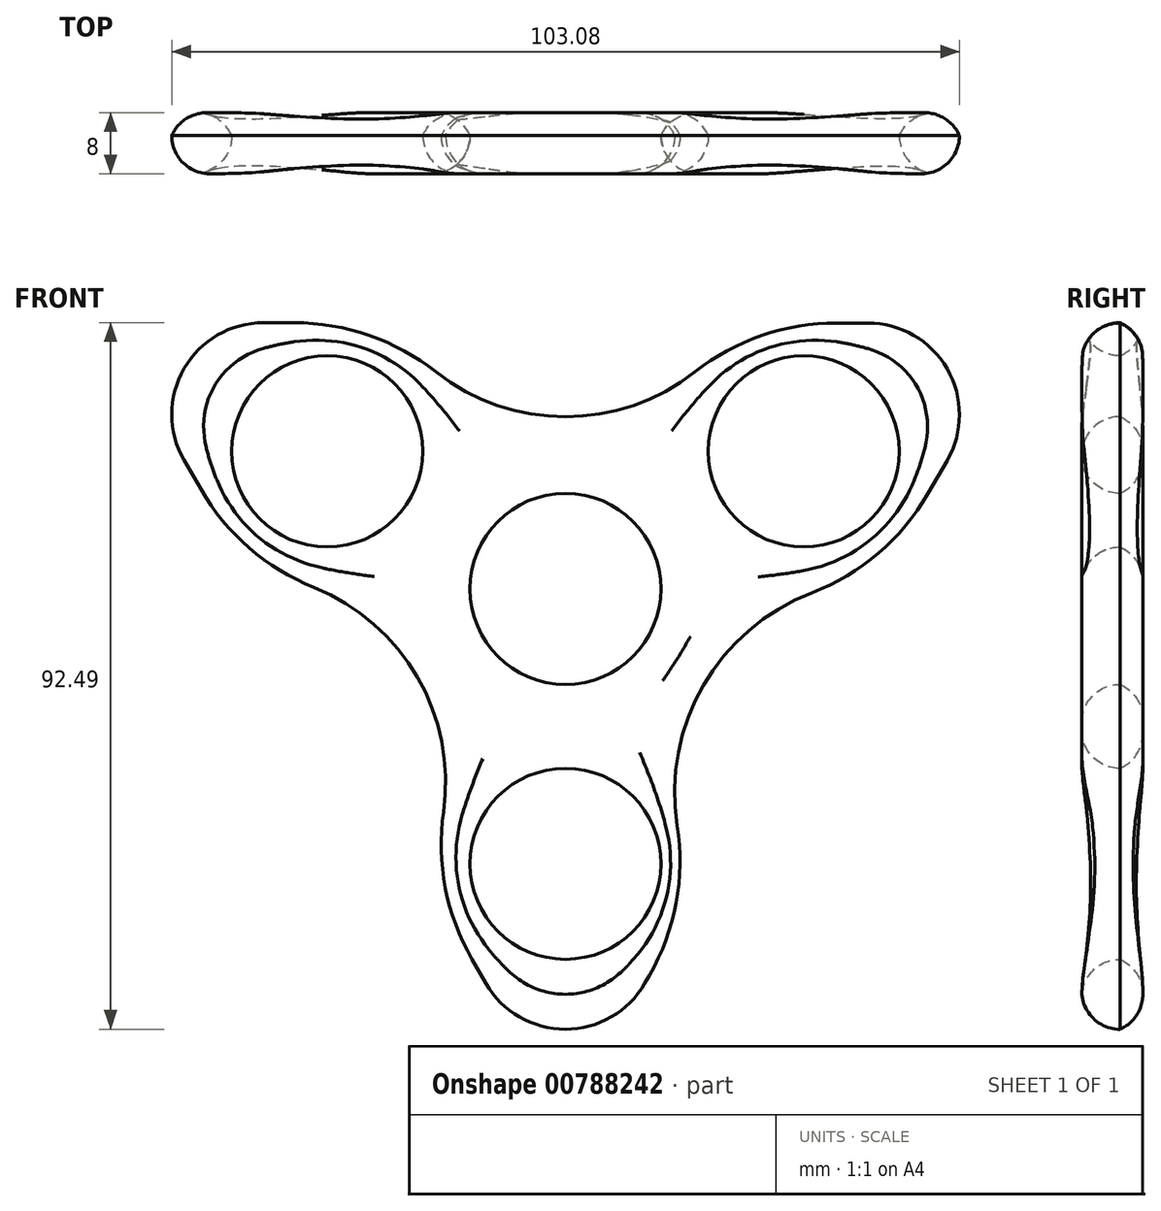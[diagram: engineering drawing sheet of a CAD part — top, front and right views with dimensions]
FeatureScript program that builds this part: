
annotation { "Feature Type Name" : "Feature", "Feature Type Description" : "" }
export const myFeature = defineFeature(function(context is Context, id is Id, definition is map)
    precondition{}
    {
        {
            var Q0;
            Q0=qCreatedBy(makeId("Front.planeOp"),FACE);
            var sketch = newSketch(context, id + "F0", { "sketchPlane" : qUnion([Q0])});
            skCircle(sketch, "E0", {"center": v(0, 0) * mm, "radius": 12.5 * mm});
            skCircle(sketch, "E1", {"center": v(31.18, 18) * mm, "radius": 12.5 * mm});
            skCircle(sketch, "E2", {"center": v(-31.18, 18) * mm, "radius": 12.5 * mm});
            skCircle(sketch, "E3", {"center": v(0, -36) * mm, "radius": 12.5 * mm});
            skCircle(sketch, "E4.cCircle", {"center": v(0, 0) * mm, "radius": 34.83 * mm, "construction": true});
            skLineSegment(sketch, "E4.0", {"start": v(49.94, 16.8) * mm, "end": v(10.37, -51.66) * mm});
            skLineSegment(sketch, "E4.1", {"start": v(-10.41, -51.65) * mm, "end": v(-49.92, 16.85) * mm});
            skLineSegment(sketch, "E4.2", {"start": v(-39.52, 34.84) * mm, "end": v(39.55, 34.81) * mm});
            skPoint(sketch, "E5", {"position": v(30.15, -17.43) * mm});
            skPoint(sketch, "E6", {"position": v(-31.7, 59.94) * mm});
            skArc(sketch, "E7.filletArc", {"start": v(-10.41, -51.65) * mm, "mid": v(-0.02, -57.65) * mm, "end": v(10.37, -51.66) * mm});
            skPoint(sketch, "E8.visualSharp", {"position": v(-24.14, 73.04) * mm});
            skArc(sketch, "E8.filletArc", {"start": v(49.94, 16.8) * mm, "mid": v(49.94, 28.8) * mm, "end": v(39.55, 34.81) * mm});
            skPoint(sketch, "E9.visualSharp", {"position": v(-60.3, 34.85) * mm});
            skArc(sketch, "E9.filletArc", {"start": v(-39.52, 34.84) * mm, "mid": v(-49.92, 28.85) * mm, "end": v(-49.92, 16.85) * mm});
            skCircle(sketch, "E10", {"center": v(42.27, -26.64) * mm, "radius": 27.98 * mm});
            skCircle(sketch, "E11", {"center": v(0, 50) * mm, "radius": 27.46 * mm});
            skCircle(sketch, "E12", {"center": v(-43.15, -25.3) * mm, "radius": 27.46 * mm});
            skCircle(sketch, "E13.cCircle", {"center": v(0, 0) * mm, "radius": 49.97 * mm, "construction": true});
            skSolve(sketch);
        }
        {
            var Q0;
            Q0=makeQuery(id+"F0.imprint","IMPRINT",FACE,{"disambiguationData":[TD([[makeQuery(id+"F0.imprint","IMPRINT",EDGE,{"derivedFrom":sQuery(id+"F0.wireOp",EDGE,"E0")}),-1.0]])]});
            extrude(context, id + "F1", {"entities" : qUnion([Q0]), "endBound" : BoundingType.SYMMETRIC, "depth" : 8 * mm, "offsetDistance" : 25 * mm});
        }
        {
            var Q0;
            {var subQ0=sQuery(id+"F0.wireOp",EDGE,"E10");var subQ1=sQuery(id+"F0.wireOp",EDGE,"E4.0");Q0=makeQuery(id+"F1.opExtrude","SWEPT_EDGE",EDGE,{"disambiguationData":[OSD([subQ1,subQ0]),TDD([makeQuery(id+"F0.imprint","INTERSECT",VERTEX,{"disambiguationData":[OD(0.0)],"derivedFrom":[subQ1,subQ0]})])]});}
            fillet(context, id + "F2", {"entities" : qUnion([Q0]), "radius" : 30 * mm, "tangentPropagation" : true, "allowEdgeOverflow" : false});
        }
        {
            var Q0;
            {var subQ0=sQuery(id+"F0.wireOp",EDGE,"E10");var subQ1=sQuery(id+"F0.wireOp",EDGE,"E4.0");Q0=makeQuery(id+"F1.opExtrude","SWEPT_EDGE",EDGE,{"disambiguationData":[OSD([subQ1,subQ0]),TDD([makeQuery(id+"F0.imprint","INTERSECT",VERTEX,{"disambiguationData":[OD(1.0)],"derivedFrom":[subQ1,subQ0]})])]});}
            var Q1;
            {var subQ0=sQuery(id+"F0.wireOp",EDGE,"E11");var subQ1=sQuery(id+"F0.wireOp",EDGE,"E4.2");Q1=makeQuery(id+"F1.opExtrude","SWEPT_EDGE",EDGE,{"disambiguationData":[OSD([subQ1,subQ0]),TDD([makeQuery(id+"F0.imprint","INTERSECT",VERTEX,{"disambiguationData":[OD(1.0)],"derivedFrom":[subQ1,subQ0]})])]});}
            var Q2;
            {var subQ0=sQuery(id+"F0.wireOp",EDGE,"E11");var subQ1=sQuery(id+"F0.wireOp",EDGE,"E4.2");Q2=makeQuery(id+"F1.opExtrude","SWEPT_EDGE",EDGE,{"disambiguationData":[OSD([subQ1,subQ0]),TDD([makeQuery(id+"F0.imprint","INTERSECT",VERTEX,{"disambiguationData":[OD(0.0)],"derivedFrom":[subQ1,subQ0]})])]});}
            var Q3;
            {var subQ0=sQuery(id+"F0.wireOp",EDGE,"E12");var subQ1=sQuery(id+"F0.wireOp",EDGE,"E4.1");Q3=makeQuery(id+"F1.opExtrude","SWEPT_EDGE",EDGE,{"disambiguationData":[OSD([subQ1,subQ0]),TDD([makeQuery(id+"F0.imprint","INTERSECT",VERTEX,{"disambiguationData":[OD(1.0)],"derivedFrom":[subQ1,subQ0]})])]});}
            var Q4;
            {var subQ0=sQuery(id+"F0.wireOp",EDGE,"E12");var subQ1=sQuery(id+"F0.wireOp",EDGE,"E4.1");Q4=makeQuery(id+"F1.opExtrude","SWEPT_EDGE",EDGE,{"disambiguationData":[OSD([subQ1,subQ0]),TDD([makeQuery(id+"F0.imprint","INTERSECT",VERTEX,{"disambiguationData":[OD(0.0)],"derivedFrom":[subQ1,subQ0]})])]});}
            fillet(context, id + "F3", {"entities" : qUnion([Q0, Q1, Q2, Q3, Q4]), "radius" : 30 * mm, "tangentPropagation" : true, "allowEdgeOverflow" : false});
        }
        {
            var Q0;
            {var subQ0=sQuery(id+"F0.wireOp",EDGE,"E10");var subQ1=sQuery(id+"F0.wireOp",EDGE,"E4.0");Q0=makeQuery(id+"F2.opFillet","BLEND_EDGE",EDGE,{"blendedFrom":[makeQuery(id+"F1.opExtrude","SWEPT_EDGE",EDGE,{"disambiguationData":[OSD([subQ1,subQ0]),TDD([makeQuery(id+"F0.imprint","INTERSECT",VERTEX,{"disambiguationData":[OD(0.0)],"derivedFrom":[subQ1,subQ0]})])]}),makeQuery(id+"F1.opExtrude","CAP_FACE",FACE,{"disambiguationData":[OSD([sQuery(id+"F0.wireOp",EDGE,"E0"),sQuery(id+"F0.wireOp",EDGE,"E1"),sQuery(id+"F0.wireOp",EDGE,"E2"),sQuery(id+"F0.wireOp",EDGE,"E3"),subQ1,sQuery(id+"F0.wireOp",EDGE,"E4.1"),sQuery(id+"F0.wireOp",EDGE,"E4.2"),sQuery(id+"F0.wireOp",EDGE,"E7.filletArc"),sQuery(id+"F0.wireOp",EDGE,"E8.filletArc"),sQuery(id+"F0.wireOp",EDGE,"E9.filletArc"),subQ0,sQuery(id+"F0.wireOp",EDGE,"E11"),sQuery(id+"F0.wireOp",EDGE,"E12")])],"isStart":false})],"blendedInto":[makeQuery(id+"F1.opExtrude","CAP_FACE",FACE,{"disambiguationData":[OSD([sQuery(id+"F0.wireOp",EDGE,"E0"),sQuery(id+"F0.wireOp",EDGE,"E1"),sQuery(id+"F0.wireOp",EDGE,"E2"),sQuery(id+"F0.wireOp",EDGE,"E3"),subQ1,sQuery(id+"F0.wireOp",EDGE,"E4.1"),sQuery(id+"F0.wireOp",EDGE,"E4.2"),sQuery(id+"F0.wireOp",EDGE,"E7.filletArc"),sQuery(id+"F0.wireOp",EDGE,"E8.filletArc"),sQuery(id+"F0.wireOp",EDGE,"E9.filletArc"),subQ0,sQuery(id+"F0.wireOp",EDGE,"E11"),sQuery(id+"F0.wireOp",EDGE,"E12")])],"isStart":false})]});}
            var Q1;
            Q1=makeQuery(id+"F1.opExtrude","CAP_FACE",FACE,{"disambiguationData":[OSD([sQuery(id+"F0.wireOp",EDGE,"E0"),sQuery(id+"F0.wireOp",EDGE,"E1"),sQuery(id+"F0.wireOp",EDGE,"E2"),sQuery(id+"F0.wireOp",EDGE,"E3"),sQuery(id+"F0.wireOp",EDGE,"E4.0"),sQuery(id+"F0.wireOp",EDGE,"E4.1"),sQuery(id+"F0.wireOp",EDGE,"E4.2"),sQuery(id+"F0.wireOp",EDGE,"E7.filletArc"),sQuery(id+"F0.wireOp",EDGE,"E8.filletArc"),sQuery(id+"F0.wireOp",EDGE,"E9.filletArc"),sQuery(id+"F0.wireOp",EDGE,"E10"),sQuery(id+"F0.wireOp",EDGE,"E11"),sQuery(id+"F0.wireOp",EDGE,"E12")])],"isStart":false});
            fillet(context, id + "F4", {"entities" : qUnion([Q0, Q1]), "radius" : 5 * mm, "tangentPropagation" : true, "allowEdgeOverflow" : false});
        }
        {
            var Q0;
            Q0=makeQuery(id+"F1.opExtrude","CAP_FACE",FACE,{"disambiguationData":[OSD([sQuery(id+"F0.wireOp",EDGE,"E0"),sQuery(id+"F0.wireOp",EDGE,"E1"),sQuery(id+"F0.wireOp",EDGE,"E2"),sQuery(id+"F0.wireOp",EDGE,"E3"),sQuery(id+"F0.wireOp",EDGE,"E4.0"),sQuery(id+"F0.wireOp",EDGE,"E4.1"),sQuery(id+"F0.wireOp",EDGE,"E4.2"),sQuery(id+"F0.wireOp",EDGE,"E7.filletArc"),sQuery(id+"F0.wireOp",EDGE,"E8.filletArc"),sQuery(id+"F0.wireOp",EDGE,"E9.filletArc"),sQuery(id+"F0.wireOp",EDGE,"E10"),sQuery(id+"F0.wireOp",EDGE,"E11"),sQuery(id+"F0.wireOp",EDGE,"E12")])],"isStart":true});
            fillet(context, id + "F5", {"entities" : qUnion([Q0]), "radius" : 5 * mm, "tangentPropagation" : true, "allowEdgeOverflow" : false});
        }
    });
